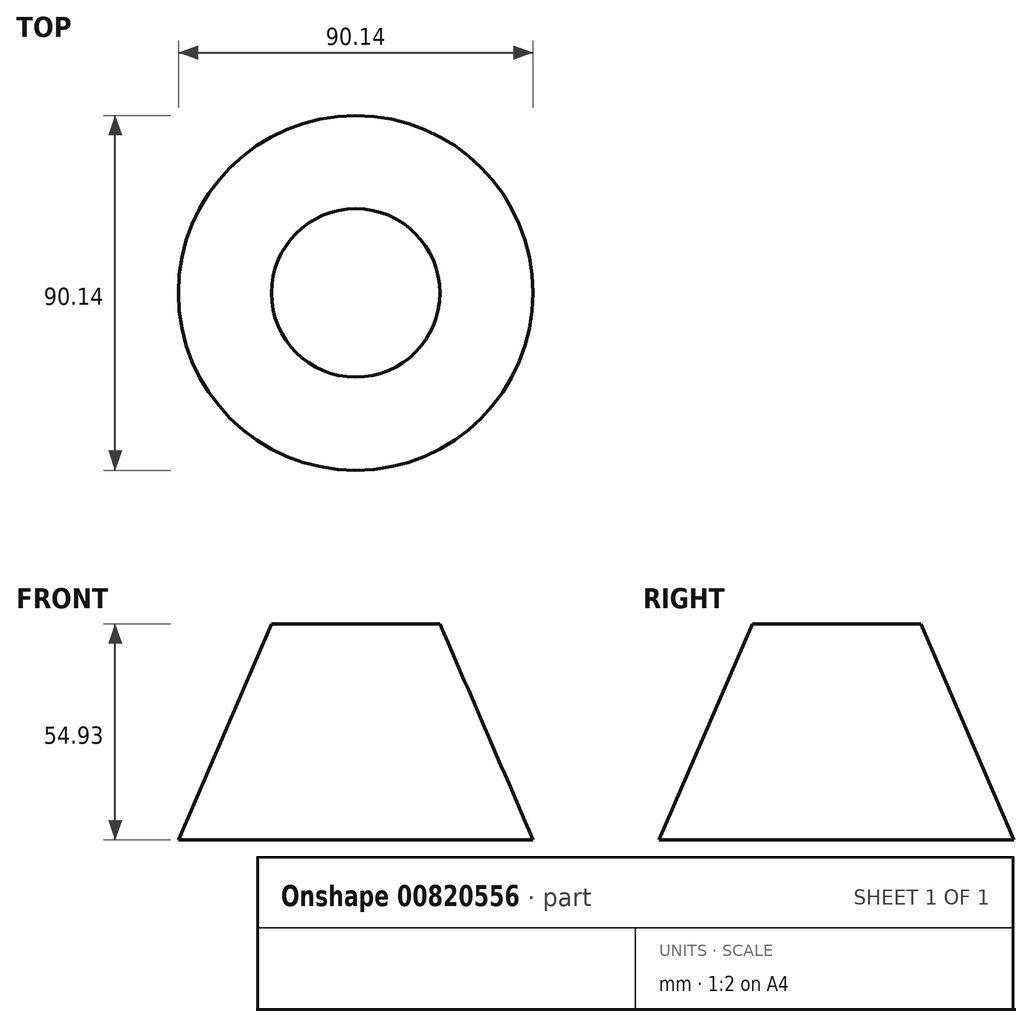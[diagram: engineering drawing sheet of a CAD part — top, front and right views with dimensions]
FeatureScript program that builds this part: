
annotation { "Feature Type Name" : "Feature", "Feature Type Description" : "" }
export const myFeature = defineFeature(function(context is Context, id is Id, definition is map)
    precondition{}
    {
        {
            var Q0;
            Q0=qCreatedBy(makeId("Front.planeOp"),FACE);
            var sketch = newSketch(context, id + "F0", { "sketchPlane" : qUnion([Q0])});
            skLineSegment(sketch, "E0", {"start": v(0, 0) * mm, "end": v(45.07, 0) * mm});
            skLineSegment(sketch, "E1", {"start": v(45.07, 0) * mm, "end": v(21.4, 54.93) * mm});
            skLineSegment(sketch, "E2", {"start": v(21.4, 54.93) * mm, "end": v(0, 54.93) * mm});
            skLineSegment(sketch, "E3", {"start": v(0, 54.93) * mm, "end": v(0, 0) * mm});
            skSolve(sketch);
        }
        {
            var Q0;
            Q0=makeQuery(id+"F0.imprint","IMPRINT",FACE,{"disambiguationData":[TD([[makeQuery(id+"F0.imprint","IMPRINT",EDGE,{"derivedFrom":sQuery(id+"F0.wireOp",EDGE,"E0")}),1.0]])]});
            var Q1;
            Q1=sQuery(id+"F0.wireOp",EDGE,"E3");
            revolve(context, id + "F1", {"surfaceOperationType" : NewSurfaceOperationType.NEW, "entities" : qUnion([Q0]), "axis" : qUnion([Q1]), "revolveType" : RevolveType.FULL});
        }
    });
